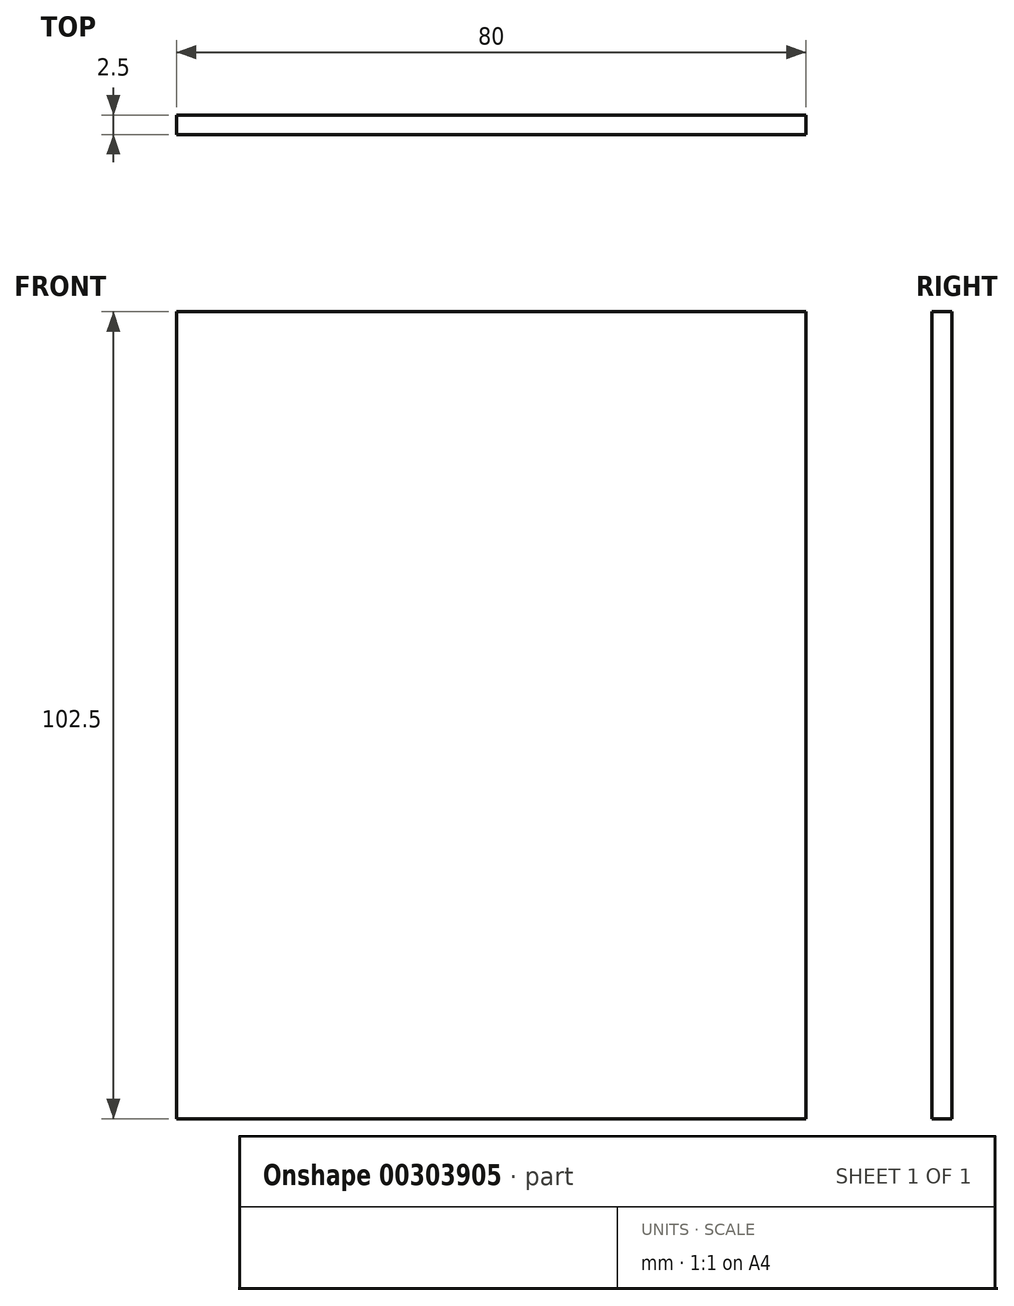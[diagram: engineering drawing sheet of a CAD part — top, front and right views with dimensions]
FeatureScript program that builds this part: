
annotation { "Feature Type Name" : "Feature", "Feature Type Description" : "" }
export const myFeature = defineFeature(function(context is Context, id is Id, definition is map)
    precondition{}
    {
        {
            var Q0;
            Q0=qCreatedBy(makeId("Front.planeOp"),FACE);
            var sketch = newSketch(context, id + "F0", { "sketchPlane" : qUnion([Q0])});
            skLineSegment(sketch, "E0.bottom", {"start": v(40, -51.25) * mm, "end": v(-40, -51.25) * mm});
            skLineSegment(sketch, "E0.top", {"start": v(40, 51.25) * mm, "end": v(-40, 51.25) * mm});
            skLineSegment(sketch, "E0.left", {"start": v(40, -51.25) * mm, "end": v(40, 51.25) * mm});
            skLineSegment(sketch, "E0.right", {"start": v(-40, -51.25) * mm, "end": v(-40, 51.25) * mm});
            skPoint(sketch, "E0.middle", {"position": v(0, 0) * mm});
            skSolve(sketch);
        }
        {
            var Q0;
            Q0=qSketchRegion(id+"F0",true);
            extrude(context, id + "F1", {"entities" : qUnion([Q0]), "depth" : 2.5 * mm});
        }
    });
